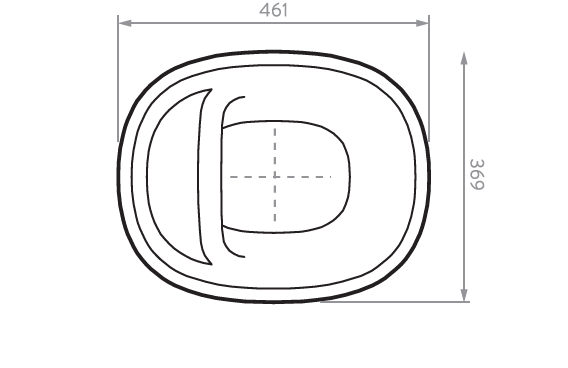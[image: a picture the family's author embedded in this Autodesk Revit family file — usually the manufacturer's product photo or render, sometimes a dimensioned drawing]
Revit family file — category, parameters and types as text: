
# Revit family: O12801001_Lavamanos Liquid Vessel
name_source: partatom
category: Plumbing Fixtures
units: mm (PartAtom-declared; Revit-internal decimal feet)

## family parameters
Cut with Voids When Loaded = No
Host = Face
OmniClass Number = 23.31.13.11
OmniClass Title = Single Sinks
Part Type = Normal
Room Calculation Point = No
Round Connector Dimension = Use Diameter
Shared = No

## types (1)
- O12801001_Lavamanos Liquid Vessel
    Alto = 140 mm  [stored 0.459318 ft]
    Ancho = 461 mm  [stored 1.51247 ft]
    Colección = Liquid
    Creado por = BIMBAU
    Default Elevation = 1219 mm
    Description = Este lavamanos fabricado 100 % en porcelana está inspirado en la fluidez del agua ya que contrasta texturas y formas orgánicas en una línea que se adapta a tu entorno. Su repisa interna en el lavamos maximiza la funcionalidad del pozo, el cual es amplio y profundo que evita el salpique y genera mayor comodidad.
    Dimensiones del Pozo = 355 x 444 mm.
    Fecha de creación = 08/04/2021
    Forma = Ovalado
    Garantía = Garantía completa para siempre en la porcelana
    Manufacturer = Corona
    Material = Corona_Porcelana_Sanitaria
    Model = Liquid Vessel
    Peso  Bruto = 9,4 kg (20,7 lbs)
    Peso neto = 8,5 kg (18,4 lbs)
    Productos Compatibles = Grifería monocontrol alta - Grifería monocontrol a pared
    Profundidad = 369 mm
    Profundidad del Pozo = 14 cm
    Referencia = O12801001
    Resistencia = Alta resistencia al rayado y cambios de temperatura
    Tipo de instalación = A pared
    URL = https://corona.co
    Uso = Residencial

note: [stored X ft] marks values corroborated as IEEE doubles in the binary element streams (Revit-internal decimal feet)

## geometry (parser evidence)
native form markers: Sweep x7
no freeform markers — native parametric forms only
